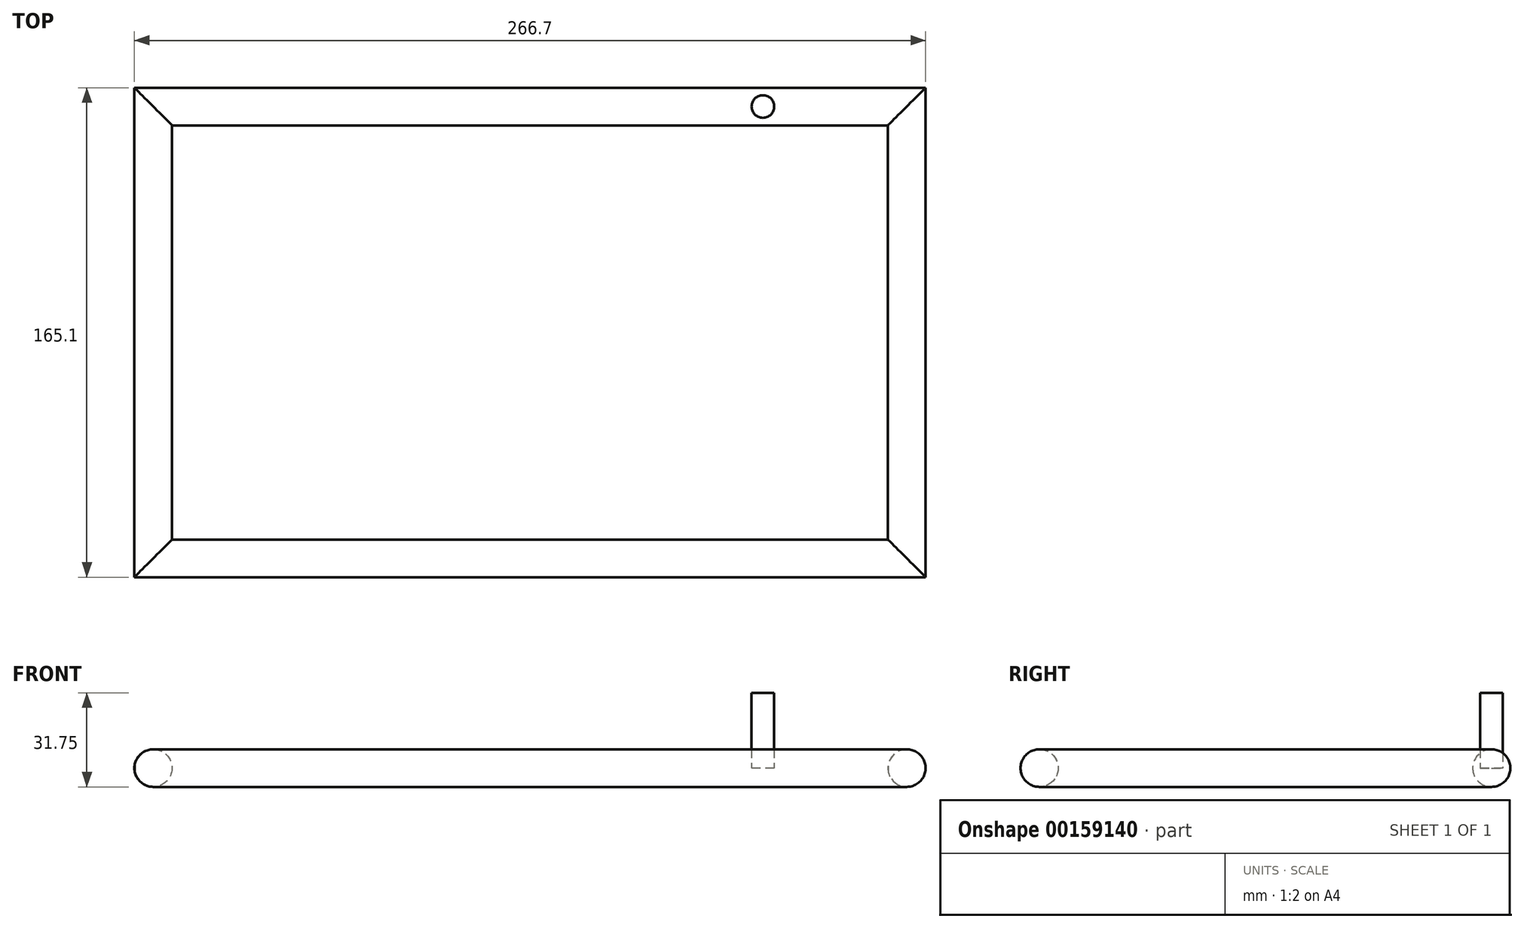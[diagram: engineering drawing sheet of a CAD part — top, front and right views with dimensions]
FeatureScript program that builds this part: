
annotation { "Feature Type Name" : "Feature", "Feature Type Description" : "" }
export const myFeature = defineFeature(function(context is Context, id is Id, definition is map)
    precondition{}
    {
        {
            var Q0;
            Q0=qCreatedBy(makeId("Right.planeOp"),FACE);
            var sketch = newSketch(context, id + "F0", { "sketchPlane" : qUnion([Q0])});
            skCircle(sketch, "E0", {"center": v(0, 0) * mm, "radius": 6.35 * mm});
            skSolve(sketch);
        }
        {
            var Q0;
            Q0=qCreatedBy(makeId("Top.planeOp"),FACE);
            var sketch = newSketch(context, id + "F1", { "sketchPlane" : qUnion([Q0])});
            skLineSegment(sketch, "E1", {"start": v(0, 0) * mm, "end": v(127, 0) * mm});
            skLineSegment(sketch, "E2", {"start": v(127, 0) * mm, "end": v(127, -152.4) * mm});
            skLineSegment(sketch, "E3", {"start": v(127, -152.4) * mm, "end": v(-127, -152.4) * mm});
            skLineSegment(sketch, "E4", {"start": v(-127, -152.4) * mm, "end": v(-127, 0) * mm});
            skLineSegment(sketch, "E5", {"start": v(-127, 0) * mm, "end": v(0, 0) * mm});
            skSolve(sketch);
        }
        {
            var Q0;
            Q0=makeQuery(id+"F0.imprint","IMPRINT",FACE,{"disambiguationData":[TD([[makeQuery(id+"F0.imprint","IMPRINT",EDGE,{"derivedFrom":sQuery(id+"F0.wireOp",EDGE,"E0")}),1.0]])]});
            var Q1;
            Q1=sQuery(id+"F1.wireOp",EDGE,"E1");
            var Q2;
            Q2=sQuery(id+"F1.wireOp",EDGE,"E2");
            var Q3;
            Q3=sQuery(id+"F1.wireOp",EDGE,"E3");
            var Q4;
            Q4=sQuery(id+"F1.wireOp",EDGE,"E4");
            var Q5;
            Q5=sQuery(id+"F1.wireOp",EDGE,"E5");
            sweep(context, id + "F2", {"profiles" : qUnion([Q0]), "path" : qUnion([Q1, Q2, Q3, Q4, Q5])});
        }
        {
            var Q0;
            Q0=qCreatedBy(makeId("Top.planeOp"),FACE);
            var sketch = newSketch(context, id + "F3", { "sketchPlane" : qUnion([Q0])});
            skCircle(sketch, "E6", {"center": v(78.51, 0) * mm, "radius": 3.81 * mm});
            skSolve(sketch);
        }
        {
            var Q0;
            Q0 = qSketchRegion(id + "F3", true);
            extrude(context, id + "F4", {"entities" : qUnion([Q0]), "depth" : 25.4 * mm});
        }
    });
